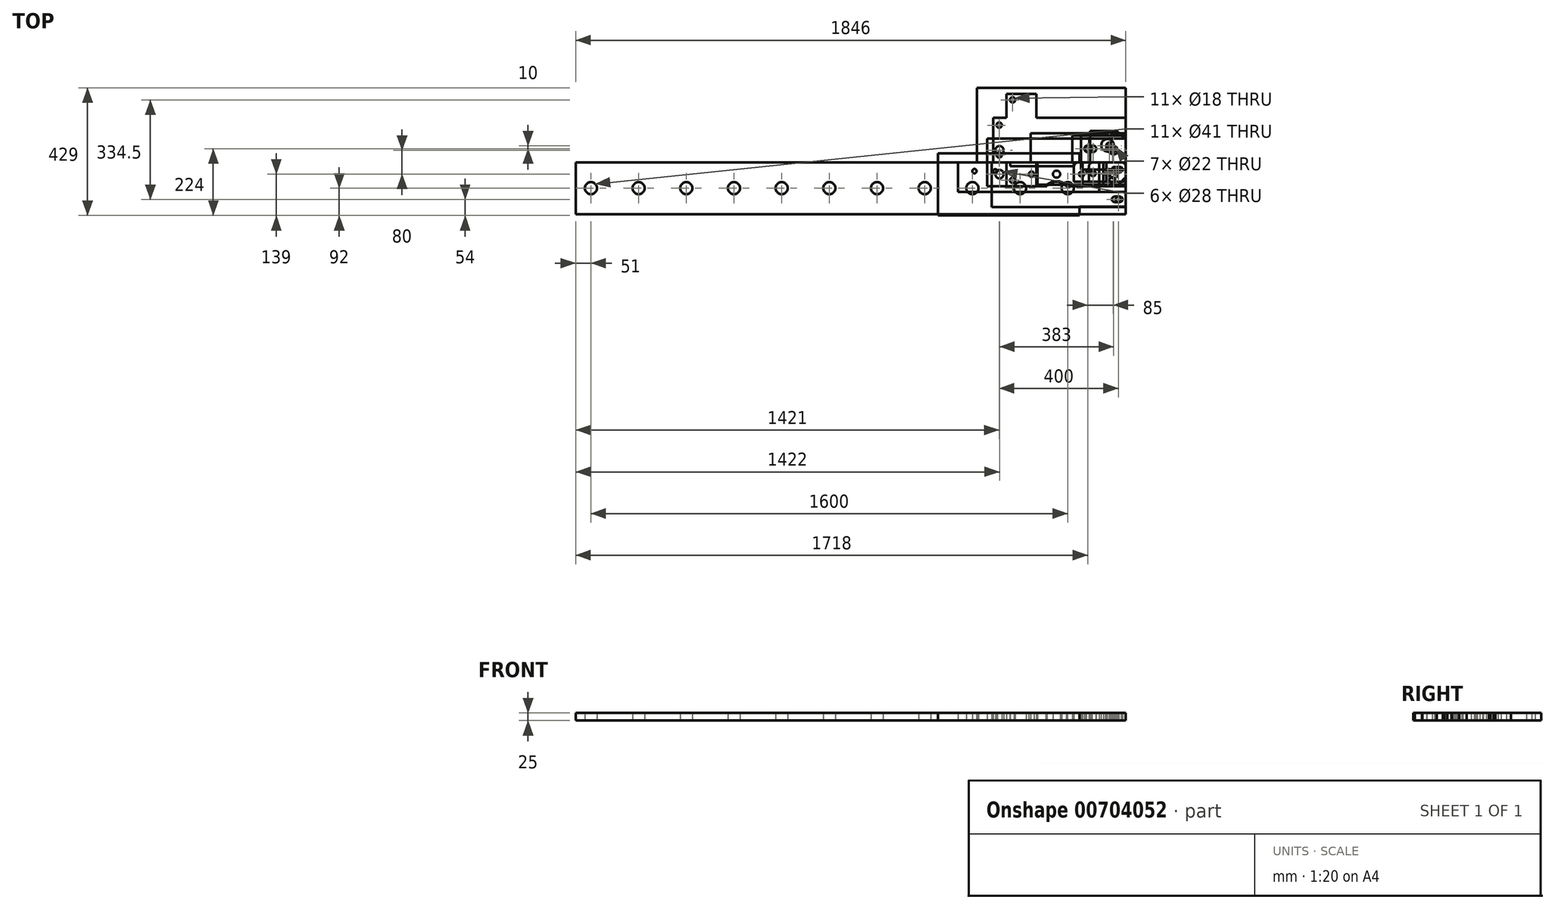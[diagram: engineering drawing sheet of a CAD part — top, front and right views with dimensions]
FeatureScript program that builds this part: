
annotation { "Feature Type Name" : "Feature", "Feature Type Description" : "" }
export const myFeature = defineFeature(function(context is Context, id is Id, definition is map)
    precondition{}
    {
        {
            var Q0;
            Q0=qCreatedBy(makeId("Top.planeOp"),FACE);
            var sketch = newSketch(context, id + "F0", { "sketchPlane" : qUnion([Q0])});
            skLineSegment(sketch, "E0.bottom", {"start": v(0, 0) * mm, "end": v(-500, 0) * mm});
            skLineSegment(sketch, "E0.top", {"start": v(0, 250) * mm, "end": v(-500, 250) * mm});
            skLineSegment(sketch, "E0.left", {"start": v(0, 0) * mm, "end": v(0, 250) * mm});
            skLineSegment(sketch, "E0.right", {"start": v(-500, 0) * mm, "end": v(-500, 250) * mm});
            skSolve(sketch);
        }
        {
            var Q0;
            Q0 = qSketchRegion(id + "F0", true);
            extrude(context, id + "F1", {"entities" : qUnion([Q0]), "depth" : 25 * mm, "offsetDistance" : 25 * mm});
        }
        {
            var Q0;
            Q0=qCreatedBy(makeId("Top.planeOp"),FACE);
            var sketch = newSketch(context, id + "F2", { "sketchPlane" : qUnion([Q0])});
            skLineSegment(sketch, "E1.bottom", {"start": v(0, 0) * mm, "end": v(-319, 0) * mm});
            skLineSegment(sketch, "E1.top", {"start": v(0, 97) * mm, "end": v(-319, 97) * mm});
            skLineSegment(sketch, "E1.left", {"start": v(0, 0) * mm, "end": v(0, 97) * mm});
            skLineSegment(sketch, "E1.right", {"start": v(-319, 0) * mm, "end": v(-319, 97) * mm});
            skSolve(sketch);
        }
        {
            var Q0;
            Q0 = qSketchRegion(id + "F2", true);
            extrude(context, id + "F3", {"entities" : qUnion([Q0]), "depth" : 25 * mm, "offsetDistance" : 25 * mm});
        }
        {
            var Q0;
            Q0=qCreatedBy(makeId("Top.planeOp"),FACE);
            var sketch = newSketch(context, id + "F4", { "sketchPlane" : qUnion([Q0])});
            skLineSegment(sketch, "E2.bottom", {"start": v(0, 0) * mm, "end": v(-123, 0) * mm});
            skLineSegment(sketch, "E2.top", {"start": v(0, 97) * mm, "end": v(-123, 97) * mm});
            skLineSegment(sketch, "E2.left", {"start": v(0, 0) * mm, "end": v(0, 97) * mm});
            skLineSegment(sketch, "E2.right", {"start": v(-123, 0) * mm, "end": v(-123, 97) * mm});
            skCircle(sketch, "E3", {"center": v(-61.5, 57) * mm, "radius": 21 * mm});
            skPoint(sketch, "E3.centerSnap0", {"position": v(-61.5, 97) * mm});
            skSolve(sketch);
        }
        {
            var Q0;
            Q0 = qSketchRegion(id + "F4", true);
            extrude(context, id + "F5", {"entities" : qUnion([Q0]), "depth" : 25 * mm, "offsetDistance" : 25 * mm});
        }
        {
            var Q0;
            Q0=qCreatedBy(makeId("Top.planeOp"),FACE);
            var sketch = newSketch(context, id + "F6", { "sketchPlane" : qUnion([Q0])});
            skLineSegment(sketch, "E4.bottom", {"start": v(0, 0) * mm, "end": v(-465, 0) * mm});
            skLineSegment(sketch, "E4.top", {"start": v(0, 80) * mm, "end": v(-465, 80) * mm});
            skLineSegment(sketch, "E4.left", {"start": v(0, 0) * mm, "end": v(0, 80) * mm});
            skLineSegment(sketch, "E4.right", {"start": v(-465, 0) * mm, "end": v(-465, 80) * mm});
            skCircle(sketch, "E5", {"center": v(-424, 40) * mm, "radius": 14 * mm});
            skPoint(sketch, "E5.centerSnap0", {"position": v(-465, 40) * mm});
            skCircle(sketch, "E6", {"center": v(-41, 40) * mm, "radius": 14 * mm});
            skSolve(sketch);
        }
        {
            var Q0;
            Q0 = qSketchRegion(id + "F6", true);
            extrude(context, id + "F7", {"entities" : qUnion([Q0]), "depth" : 25 * mm, "offsetDistance" : 25 * mm});
        }
        {
            var Q0;
            Q0=qCreatedBy(makeId("Top.planeOp"),FACE);
            var sketch = newSketch(context, id + "F8", { "sketchPlane" : qUnion([Q0])});
            skLineSegment(sketch, "E7", {"start": v(0, 0) * mm, "end": v(-300, 0) * mm});
            skLineSegment(sketch, "E8", {"start": v(-300, 0) * mm, "end": v(-300, -80.5) * mm});
            skLineSegment(sketch, "E9", {"start": v(-300, -80.5) * mm, "end": v(-400, -80.5) * mm});
            skLineSegment(sketch, "E10", {"start": v(-400, -80.5) * mm, "end": v(-400, 0) * mm});
            skLineSegment(sketch, "E11", {"start": v(-400, 0) * mm, "end": v(-445, 0) * mm});
            skLineSegment(sketch, "E12", {"start": v(-445, 0) * mm, "end": v(-445, 149) * mm});
            skLineSegment(sketch, "E13", {"start": v(-445, 149) * mm, "end": v(-400, 149) * mm});
            skLineSegment(sketch, "E14", {"start": v(-400, 149) * mm, "end": v(-400, 229.5) * mm});
            skLineSegment(sketch, "E15", {"start": v(-400, 229.5) * mm, "end": v(-300, 229.5) * mm});
            skLineSegment(sketch, "E16", {"start": v(-300, 229.5) * mm, "end": v(-300, 149) * mm});
            skLineSegment(sketch, "E17", {"start": v(-300, 149) * mm, "end": v(0, 149) * mm});
            skLineSegment(sketch, "E18", {"start": v(0, 149) * mm, "end": v(0, 0) * mm});
            skCircle(sketch, "E19", {"center": v(-380, 209.5) * mm, "radius": 9 * mm});
            skCircle(sketch, "E20", {"center": v(-380, -60.5) * mm, "radius": 9 * mm});
            skCircle(sketch, "E21", {"center": v(-425, 124.5) * mm, "radius": 9 * mm});
            skCircle(sketch, "E22", {"center": v(-425, 24.5) * mm, "radius": 9 * mm});
            skSolve(sketch);
        }
        {
            var Q0;
            Q0 = qSketchRegion(id + "F8", true);
            extrude(context, id + "F9", {"entities" : qUnion([Q0]), "depth" : 25 * mm, "offsetDistance" : 25 * mm});
        }
        {
            var Q0;
            Q0=qCreatedBy(makeId("Top.planeOp"),FACE);
            var sketch = newSketch(context, id + "F10", { "sketchPlane" : qUnion([Q0])});
            skLineSegment(sketch, "E23.bottom", {"start": v(0, 0) * mm, "end": v(-450, 0) * mm});
            skLineSegment(sketch, "E23.top", {"start": v(0, -150) * mm, "end": v(-450, -150) * mm});
            skLineSegment(sketch, "E23.left", {"start": v(0, 0) * mm, "end": v(0, -150) * mm});
            skLineSegment(sketch, "E23.right", {"start": v(-450, 0) * mm, "end": v(-450, -150) * mm});
            skCircle(sketch, "E24", {"center": v(-25, -25) * mm, "radius": 9 * mm});
            skCircle(sketch, "E25", {"center": v(-25, -125) * mm, "radius": 9 * mm});
            skSolve(sketch);
        }
        {
            var Q0;
            Q0 = qSketchRegion(id + "F10", true);
            extrude(context, id + "F11", {"entities" : qUnion([Q0]), "depth" : 25 * mm, "offsetDistance" : 25 * mm});
        }
        {
            var Q0;
            Q0=qCreatedBy(makeId("Top.planeOp"),FACE);
            var sketch = newSketch(context, id + "F12", { "sketchPlane" : qUnion([Q0])});
            skLineSegment(sketch, "E26.bottom", {"start": v(0, 0) * mm, "end": v(-150, 0) * mm});
            skLineSegment(sketch, "E26.top", {"start": v(0, -25) * mm, "end": v(-150, -25) * mm});
            skLineSegment(sketch, "E26.left", {"start": v(0, 0) * mm, "end": v(0, -25) * mm});
            skLineSegment(sketch, "E26.right", {"start": v(-150, 0) * mm, "end": v(-150, -25) * mm});
            skSolve(sketch);
        }
        {
            var Q0;
            Q0 = qSketchRegion(id + "F12", true);
            extrude(context, id + "F13", {"entities" : qUnion([Q0]), "depth" : 25 * mm, "offsetDistance" : 25 * mm});
        }
        {
            var Q0;
            Q0=qCreatedBy(makeId("Top.planeOp"),FACE);
            var sketch = newSketch(context, id + "F14", { "sketchPlane" : qUnion([Q0])});
            skLineSegment(sketch, "E27", {"start": v(0, 0) * mm, "end": v(-155, 0) * mm});
            skLineSegment(sketch, "E28", {"start": v(-155, 0) * mm, "end": v(-155, 30) * mm});
            skLineSegment(sketch, "E29", {"start": v(-155, 30) * mm, "end": v(-630, 30) * mm});
            skLineSegment(sketch, "E30", {"start": v(-630, 30) * mm, "end": v(-630, -179) * mm});
            skLineSegment(sketch, "E31", {"start": v(-630, -179) * mm, "end": v(-155, -179) * mm});
            skLineSegment(sketch, "E32", {"start": v(-155, -179) * mm, "end": v(-155, -149) * mm});
            skLineSegment(sketch, "E33", {"start": v(-155, -149) * mm, "end": v(0, -149) * mm});
            skLineSegment(sketch, "E34", {"start": v(0, -149) * mm, "end": v(0, 0) * mm});
            skArc(sketch, "E35", {"start": v(-20, -33.5) * mm, "mid": v(-11, -24.5) * mm, "end": v(-20, -15.5) * mm});
            skArc(sketch, "E36", {"start": v(-38, -15.5) * mm, "mid": v(-47, -24.5) * mm, "end": v(-38, -33.5) * mm});
            skArc(sketch, "E37", {"start": v(-20, -133.5) * mm, "mid": v(-11, -124.5) * mm, "end": v(-20, -115.5) * mm});
            skArc(sketch, "E38", {"start": v(-38, -115.5) * mm, "mid": v(-47, -124.5) * mm, "end": v(-38, -133.5) * mm});
            skLineSegment(sketch, "E39", {"start": v(-38, -15.5) * mm, "end": v(-20, -15.5) * mm});
            skLineSegment(sketch, "E40", {"start": v(-38, -33.5) * mm, "end": v(-20, -33.5) * mm});
            skLineSegment(sketch, "E41", {"start": v(-38, -115.5) * mm, "end": v(-20, -115.5) * mm});
            skLineSegment(sketch, "E42", {"start": v(-38, -133.5) * mm, "end": v(-20, -133.5) * mm});
            skSolve(sketch);
        }
        {
            var Q0;
            Q0 = qSketchRegion(id + "F14", true);
            extrude(context, id + "F15", {"entities" : qUnion([Q0]), "depth" : 25 * mm, "offsetDistance" : 25 * mm});
        }
        {
            var Q0;
            Q0=qCreatedBy(makeId("Top.planeOp"),FACE);
            var sketch = newSketch(context, id + "F16", { "sketchPlane" : qUnion([Q0])});
            skLineSegment(sketch, "E43.bottom", {"start": v(0, 0) * mm, "end": v(-180, 0) * mm});
            skLineSegment(sketch, "E43.top", {"start": v(0, 90) * mm, "end": v(-180, 90) * mm});
            skLineSegment(sketch, "E43.left", {"start": v(0, 0) * mm, "end": v(0, 90) * mm});
            skLineSegment(sketch, "E43.right", {"start": v(-180, 0) * mm, "end": v(-180, 90) * mm});
            skCircle(sketch, "E44", {"center": v(-125, 45) * mm, "radius": 11 * mm});
            skPoint(sketch, "E44.centerSnap0", {"position": v(-180, 45) * mm});
            skCircle(sketch, "E45", {"center": v(-55, 45) * mm, "radius": 11 * mm});
            skSolve(sketch);
        }
        {
            var Q0;
            Q0 = qSketchRegion(id + "F16", true);
            extrude(context, id + "F17", {"entities" : qUnion([Q0]), "depth" : 25 * mm, "offsetDistance" : 25 * mm});
        }
        {
            var Q0;
            Q0=qCreatedBy(makeId("Top.planeOp"),FACE);
            var sketch = newSketch(context, id + "F18", { "sketchPlane" : qUnion([Q0])});
            skLineSegment(sketch, "E46.bottom", {"start": v(0, 0) * mm, "end": v(-150, 0) * mm});
            skLineSegment(sketch, "E46.top", {"start": v(0, 90) * mm, "end": v(-150, 90) * mm});
            skLineSegment(sketch, "E46.left", {"start": v(0, 0) * mm, "end": v(0, 90) * mm});
            skLineSegment(sketch, "E46.right", {"start": v(-150, 0) * mm, "end": v(-150, 90) * mm});
            skCircle(sketch, "E47", {"center": v(-110, 45) * mm, "radius": 11 * mm});
            skPoint(sketch, "E47.centerSnap0", {"position": v(-150, 45) * mm});
            skCircle(sketch, "E48", {"center": v(-45, 45) * mm, "radius": 11 * mm});
            skSolve(sketch);
        }
        {
            var Q0;
            Q0 = qSketchRegion(id + "F18", true);
            extrude(context, id + "F19", {"entities" : qUnion([Q0]), "depth" : 25 * mm, "offsetDistance" : 25 * mm});
        }
        {
            var Q0;
            Q0=qCreatedBy(makeId("Top.planeOp"),FACE);
            var sketch = newSketch(context, id + "F20", { "sketchPlane" : qUnion([Q0])});
            skLineSegment(sketch, "E49.bottom", {"start": v(0, 0) * mm, "end": v(-180, 0) * mm});
            skLineSegment(sketch, "E49.top", {"start": v(0, 90) * mm, "end": v(-180, 90) * mm});
            skLineSegment(sketch, "E49.left", {"start": v(0, 0) * mm, "end": v(0, 90) * mm});
            skLineSegment(sketch, "E49.right", {"start": v(-180, 0) * mm, "end": v(-180, 90) * mm});
            skCircle(sketch, "E50", {"center": v(-128, 45) * mm, "radius": 11 * mm});
            skPoint(sketch, "E50.centerSnap0", {"position": v(-180, 45) * mm});
            skCircle(sketch, "E51", {"center": v(-43, 45) * mm, "radius": 11 * mm});
            skSolve(sketch);
        }
        {
            var Q0;
            Q0 = qSketchRegion(id + "F20", true);
            extrude(context, id + "F21", {"entities" : qUnion([Q0]), "depth" : 25 * mm, "offsetDistance" : 25 * mm});
        }
        {
            var Q0;
            Q0=qCreatedBy(makeId("Top.planeOp"),FACE);
            var sketch = newSketch(context, id + "F22", { "sketchPlane" : qUnion([Q0])});
            skLineSegment(sketch, "E52.bottom", {"start": v(-15, 0) * mm, "end": v(-109, 0) * mm});
            skLineSegment(sketch, "E52.top", {"start": v(0, -65) * mm, "end": v(-124, -65) * mm});
            skLineSegment(sketch, "E52.left", {"start": v(0, -15) * mm, "end": v(0, -65) * mm});
            skLineSegment(sketch, "E52.right", {"start": v(-124, -15) * mm, "end": v(-124, -65) * mm});
            skPoint(sketch, "E53.visualSharp", {"position": v(-124, 0) * mm});
            skArc(sketch, "E53.filletArc", {"start": v(-109, 0) * mm, "mid": v(-119.6, -4.4) * mm, "end": v(-124, -15) * mm});
            skPoint(sketch, "E54.visualSharp", {"position": v(0, 0) * mm});
            skArc(sketch, "E54.filletArc", {"start": v(0, -15) * mm, "mid": v(-4.4, -4.4) * mm, "end": v(-15, 0) * mm});
            skSolve(sketch);
        }
        {
            var Q0;
            Q0 = qSketchRegion(id + "F22", true);
            extrude(context, id + "F23", {"entities" : qUnion([Q0]), "depth" : 25 * mm, "offsetDistance" : 25 * mm});
        }
        {
            var Q0;
            Q0=qCreatedBy(makeId("Top.planeOp"),FACE);
            var sketch = newSketch(context, id + "F24", { "sketchPlane" : qUnion([Q0])});
            skLineSegment(sketch, "E55.bottom", {"start": v(-15, 0) * mm, "end": v(-159, 0) * mm});
            skLineSegment(sketch, "E55.top", {"start": v(0, -65) * mm, "end": v(-174, -65) * mm});
            skLineSegment(sketch, "E55.left", {"start": v(0, -15) * mm, "end": v(0, -65) * mm});
            skLineSegment(sketch, "E55.right", {"start": v(-174, -15) * mm, "end": v(-174, -65) * mm});
            skPoint(sketch, "E56.visualSharp", {"position": v(-174, 0) * mm});
            skArc(sketch, "E56.filletArc", {"start": v(-159, 0) * mm, "mid": v(-169.6, -4.4) * mm, "end": v(-174, -15) * mm});
            skPoint(sketch, "E57.visualSharp", {"position": v(0, 0) * mm});
            skArc(sketch, "E57.filletArc", {"start": v(0, -15) * mm, "mid": v(-4.4, -4.4) * mm, "end": v(-15, 0) * mm});
            skSolve(sketch);
        }
        {
            var Q0;
            Q0 = qSketchRegion(id + "F24", true);
            extrude(context, id + "F25", {"entities" : qUnion([Q0]), "depth" : 25 * mm, "offsetDistance" : 25 * mm});
        }
        {
            var Q0;
            Q0=qCreatedBy(makeId("Top.planeOp"),FACE);
            var sketch = newSketch(context, id + "F26", { "sketchPlane" : qUnion([Q0])});
            skLineSegment(sketch, "E58.bottom", {"start": v(0, 0) * mm, "end": v(-1846, 0) * mm});
            skLineSegment(sketch, "E58.top", {"start": v(0, -174) * mm, "end": v(-1846, -174) * mm});
            skLineSegment(sketch, "E58.left", {"start": v(0, 0) * mm, "end": v(0, -174) * mm});
            skLineSegment(sketch, "E58.right", {"start": v(-1846, 0) * mm, "end": v(-1846, -174) * mm});
            skCircle(sketch, "E59", {"center": v(-195, -87) * mm, "radius": 20.5 * mm});
            skPoint(sketch, "E59.centerSnap0", {"position": v(0, -87) * mm});
            skCircle(sketch, "E60", {"center": v(-355, -87) * mm, "radius": 20.5 * mm});
            skCircle(sketch, "E61", {"center": v(-515, -87) * mm, "radius": 20.5 * mm});
            skCircle(sketch, "E62", {"center": v(-675, -87) * mm, "radius": 20.5 * mm});
            skCircle(sketch, "E63.MirrorC", {"center": v(-835, -87) * mm, "radius": 20.5 * mm});
            skCircle(sketch, "E64.MirrorC", {"center": v(-995, -87) * mm, "radius": 20.5 * mm});
            skCircle(sketch, "E65.MirrorC", {"center": v(-1155, -87) * mm, "radius": 20.5 * mm});
            skPoint(sketch, "E66.orphan", {"position": v(-675, 55.79) * mm});
            skCircle(sketch, "E67.MirrorC", {"center": v(-1315, -87) * mm, "radius": 20.5 * mm});
            skCircle(sketch, "E68.MirrorC", {"center": v(-1475, -87) * mm, "radius": 20.5 * mm});
            skCircle(sketch, "E69.MirrorC", {"center": v(-1635, -87) * mm, "radius": 20.5 * mm});
            skCircle(sketch, "E70.MirrorC", {"center": v(-1795, -87) * mm, "radius": 20.5 * mm});
            skPoint(sketch, "E71.orphan", {"position": v(-1155, 39.2) * mm});
            skSolve(sketch);
        }
        {
            var Q0;
            Q0 = qSketchRegion(id + "F26", true);
            extrude(context, id + "F27", {"entities" : qUnion([Q0]), "depth" : 25 * mm, "offsetDistance" : 25 * mm});
        }
        {
            var Q0;
            Q0=qCreatedBy(makeId("Top.planeOp"),FACE);
            var sketch = newSketch(context, id + "F28", { "sketchPlane" : qUnion([Q0])});
            skLineSegment(sketch, "E72.bottom", {"start": v(0, 0) * mm, "end": v(-145, 0) * mm});
            skLineSegment(sketch, "E72.top", {"start": v(0, -76) * mm, "end": v(-145, -76) * mm});
            skLineSegment(sketch, "E72.left", {"start": v(0, 0) * mm, "end": v(0, -76) * mm});
            skLineSegment(sketch, "E72.right", {"start": v(-145, 0) * mm, "end": v(-145, -76) * mm});
            skCircle(sketch, "E73", {"center": v(-110, -38) * mm, "radius": 9 * mm});
            skPoint(sketch, "E73.centerSnap0", {"position": v(-145, -38) * mm});
            skCircle(sketch, "E74", {"center": v(-60, -38) * mm, "radius": 9 * mm});
            skSolve(sketch);
        }
        {
            var Q0;
            Q0 = qSketchRegion(id + "F28", true);
            extrude(context, id + "F29", {"entities" : qUnion([Q0]), "depth" : 25 * mm, "offsetDistance" : 25 * mm});
        }
        {
            var Q0;
            Q0=qCreatedBy(makeId("Top.planeOp"),FACE);
            var sketch = newSketch(context, id + "F30", { "sketchPlane" : qUnion([Q0])});
            skLineSegment(sketch, "E75.bottom", {"start": v(0, 0) * mm, "end": v(-297, 0) * mm});
            skLineSegment(sketch, "E75.top", {"start": v(0, -75) * mm, "end": v(-297, -75) * mm});
            skLineSegment(sketch, "E75.left", {"start": v(0, 0) * mm, "end": v(0, -75) * mm});
            skLineSegment(sketch, "E75.right", {"start": v(-297, 0) * mm, "end": v(-297, -75) * mm});
            skSolve(sketch);
        }
        {
            var Q0;
            Q0 = qSketchRegion(id + "F30", true);
            extrude(context, id + "F31", {"entities" : qUnion([Q0]), "depth" : 25 * mm, "offsetDistance" : 25 * mm});
        }
        {
            var Q0;
            Q0=qCreatedBy(makeId("Top.planeOp"),FACE);
            var sketch = newSketch(context, id + "F32", { "sketchPlane" : qUnion([Q0])});
            skLineSegment(sketch, "E76.bottom", {"start": v(0, 0) * mm, "end": v(-75, 0) * mm});
            skLineSegment(sketch, "E76.top", {"start": v(-25, -75) * mm, "end": v(-75, -75) * mm});
            skLineSegment(sketch, "E76.left", {"start": v(0, 0) * mm, "end": v(0, -50) * mm});
            skLineSegment(sketch, "E76.right", {"start": v(-75, 0) * mm, "end": v(-75, -75) * mm});
            skLineSegment(sketch, "E77", {"start": v(0, -50) * mm, "end": v(-25, -75) * mm});
            skPoint(sketch, "E78.orphan", {"position": v(0, -75) * mm});
            skSolve(sketch);
        }
        {
            var Q0;
            Q0 = qSketchRegion(id + "F32", true);
            extrude(context, id + "F33", {"entities" : qUnion([Q0]), "depth" : 25 * mm, "offsetDistance" : 25 * mm});
        }
        {
            var Q0;
            Q0=qCreatedBy(makeId("Top.planeOp"),FACE);
            var sketch = newSketch(context, id + "F34", { "sketchPlane" : qUnion([Q0])});
            skLineSegment(sketch, "E79.bottom", {"start": v(0, 0) * mm, "end": v(-65, 0) * mm});
            skLineSegment(sketch, "E79.top", {"start": v(0, -65) * mm, "end": v(-65, -65) * mm});
            skLineSegment(sketch, "E79.left", {"start": v(0, 0) * mm, "end": v(0, -65) * mm});
            skLineSegment(sketch, "E79.right", {"start": v(-65, 0) * mm, "end": v(-65, -65) * mm});
            skCircle(sketch, "E80", {"center": v(-32.5, -32.5) * mm, "radius": 9 * mm});
            skPoint(sketch, "E80.centerSnap0", {"position": v(-65, -32.5) * mm});
            skPoint(sketch, "E80.centerSnap1", {"position": v(-32.5, 0) * mm});
            skSolve(sketch);
        }
        {
            var Q0;
            Q0 = qSketchRegion(id + "F34", true);
            extrude(context, id + "F35", {"entities" : qUnion([Q0]), "depth" : 25 * mm, "offsetDistance" : 25 * mm});
        }
        {
            var Q0;
            Q0=qCreatedBy(makeId("Top.planeOp"),FACE);
            var sketch = newSketch(context, id + "F36", { "sketchPlane" : qUnion([Q0])});
            skLineSegment(sketch, "E81.bottom", {"start": v(0, 0) * mm, "end": v(-175, 0) * mm});
            skLineSegment(sketch, "E81.top", {"start": v(0, -100) * mm, "end": v(-563, -100) * mm});
            skLineSegment(sketch, "E81.left", {"start": v(0, 0) * mm, "end": v(0, -100) * mm});
            skLineSegment(sketch, "E81.right", {"start": v(-563, 0) * mm, "end": v(-563, -100) * mm});
            skLineSegment(sketch, "E82", {"start": v(-388, 0) * mm, "end": v(-388, -13) * mm});
            skLineSegment(sketch, "E83", {"start": v(-388, -13) * mm, "end": v(-175, -13) * mm});
            skLineSegment(sketch, "E84", {"start": v(-175, -13) * mm, "end": v(-175, 0) * mm});
            skLineSegment(sketch, "E85.trimOffspring", {"start": v(-388, 0) * mm, "end": v(-563, 0) * mm});
            skCircle(sketch, "E86", {"center": v(-508, -30) * mm, "radius": 7.35 * mm});
            skCircle(sketch, "E87", {"center": v(-438, -30) * mm, "radius": 6.78 * mm});
            skCircle(sketch, "E88", {"center": v(-125, -30) * mm, "radius": 7.5 * mm});
            skCircle(sketch, "E89", {"center": v(-55, -30) * mm, "radius": 7.13 * mm});
            skSolve(sketch);
        }
        {
            var Q0;
            Q0 = qSketchRegion(id + "F36", true);
            extrude(context, id + "F37", {"entities" : qUnion([Q0]), "depth" : 25 * mm, "offsetDistance" : 25 * mm});
        }
        {
            var Q0;
            Q0=qCreatedBy(makeId("Top.planeOp"),FACE);
            var sketch = newSketch(context, id + "F38", { "sketchPlane" : qUnion([Q0])});
            skLineSegment(sketch, "E90", {"start": v(0, 0) * mm, "end": v(0, 75) * mm});
            skLineSegment(sketch, "E91", {"start": v(0, 75) * mm, "end": v(-30, 105) * mm});
            skLineSegment(sketch, "E92", {"start": v(-30, 105) * mm, "end": v(-120, 105) * mm});
            skLineSegment(sketch, "E93", {"start": v(-120, 105) * mm, "end": v(-120, 0) * mm});
            skLineSegment(sketch, "E94", {"start": v(-120, 0) * mm, "end": v(0, 0) * mm});
            skCircle(sketch, "E95", {"center": v(-55, 55) * mm, "radius": 11 * mm});
            skSolve(sketch);
        }
        {
            var Q0;
            Q0 = qSketchRegion(id + "F38", true);
            extrude(context, id + "F39", {"entities" : qUnion([Q0]), "depth" : 25 * mm, "offsetDistance" : 25 * mm});
        }
        {
            var Q0;
            Q0=qCreatedBy(makeId("Top.planeOp"),FACE);
            var sketch = newSketch(context, id + "F40", { "sketchPlane" : qUnion([Q0])});
            skLineSegment(sketch, "E96.bottom", {"start": v(0, 0) * mm, "end": v(-90, 0) * mm});
            skLineSegment(sketch, "E96.top", {"start": v(0, -100) * mm, "end": v(-90, -100) * mm});
            skLineSegment(sketch, "E96.left", {"start": v(0, 0) * mm, "end": v(0, -100) * mm});
            skLineSegment(sketch, "E96.right", {"start": v(-90, 0) * mm, "end": v(-90, -100) * mm});
            skCircle(sketch, "E97", {"center": v(-45, -60) * mm, "radius": 10 * mm});
            skPoint(sketch, "E97.centerSnap0", {"position": v(-45, 0) * mm});
            skSolve(sketch);
        }
        {
            var Q0;
            Q0 = qSketchRegion(id + "F40", true);
            extrude(context, id + "F41", {"entities" : qUnion([Q0]), "depth" : 25 * mm, "offsetDistance" : 25 * mm});
        }
        {
            var Q0;
            Q0=qCreatedBy(makeId("Top.planeOp"),FACE);
            var sketch = newSketch(context, id + "F42", { "sketchPlane" : qUnion([Q0])});
            skLineSegment(sketch, "E98.bottom", {"start": v(0, 0) * mm, "end": v(-465, 0) * mm});
            skLineSegment(sketch, "E98.top", {"start": v(0, -80) * mm, "end": v(-200.32, -80) * mm});
            skLineSegment(sketch, "E98.left", {"start": v(0, 0) * mm, "end": v(0, -80) * mm});
            skLineSegment(sketch, "E98.right", {"start": v(-465, 0) * mm, "end": v(-465, -80) * mm});
            skCircle(sketch, "E99", {"center": v(-232.5, -40) * mm, "radius": 12 * mm});
            skPoint(sketch, "E99.centerSnap0", {"position": v(-232.5, -80) * mm});
            skCircle(sketch, "E100", {"center": v(-424, -40) * mm, "radius": 14 * mm});
            skCircle(sketch, "E101", {"center": v(-41, -40) * mm, "radius": 14 * mm});
            skArc(sketch, "E102", {"start": v(-200.32, -80) * mm, "mid": v(-232.5, -65.34) * mm, "end": v(-264.68, -80) * mm});
            skLineSegment(sketch, "E103.trimOffspring", {"start": v(-264.68, -80) * mm, "end": v(-465, -80) * mm});
            skSolve(sketch);
        }
        {
            var Q0;
            Q0 = qSketchRegion(id + "F42", true);
            extrude(context, id + "F43", {"entities" : qUnion([Q0]), "depth" : 25 * mm, "offsetDistance" : 25 * mm});
        }
        {
            var Q0;
            Q0=qCreatedBy(makeId("Top.planeOp"),FACE);
            var sketch = newSketch(context, id + "F44", { "sketchPlane" : qUnion([Q0])});
            skLineSegment(sketch, "E104.bottom", {"start": v(0, 0) * mm, "end": v(-465, 0) * mm});
            skLineSegment(sketch, "E104.top", {"start": v(0, -80) * mm, "end": v(-196.42, -80) * mm});
            skLineSegment(sketch, "E104.left", {"start": v(0, 0) * mm, "end": v(0, -80) * mm});
            skLineSegment(sketch, "E104.right", {"start": v(-465, 0) * mm, "end": v(-465, -80) * mm});
            skCircle(sketch, "E105", {"center": v(-232.5, -40) * mm, "radius": 12 * mm});
            skPoint(sketch, "E105.centerSnap0", {"position": v(-465, -40) * mm});
            skPoint(sketch, "E105.centerSnap1", {"position": v(-232.5, 0) * mm});
            skCircle(sketch, "E106", {"center": v(-316.5, -40) * mm, "radius": 9 * mm});
            skCircle(sketch, "E107", {"center": v(-424, -40) * mm, "radius": 14 * mm});
            skCircle(sketch, "E108", {"center": v(-148.5, -40) * mm, "radius": 9 * mm});
            skCircle(sketch, "E109", {"center": v(-41, -40) * mm, "radius": 14 * mm});
            skArc(sketch, "E110", {"start": v(-196.42, -80) * mm, "mid": v(-232.5, -63.64) * mm, "end": v(-268.58, -80) * mm});
            skPoint(sketch, "E110.centerSnap0", {"position": v(-232.5, -80) * mm});
            skLineSegment(sketch, "E111.trimOffspring", {"start": v(-268.58, -80) * mm, "end": v(-465, -80) * mm});
            skSolve(sketch);
        }
        {
            var Q0;
            Q0 = qSketchRegion(id + "F44", true);
            extrude(context, id + "F45", {"entities" : qUnion([Q0]), "depth" : 25 * mm, "offsetDistance" : 25 * mm});
        }
    });
